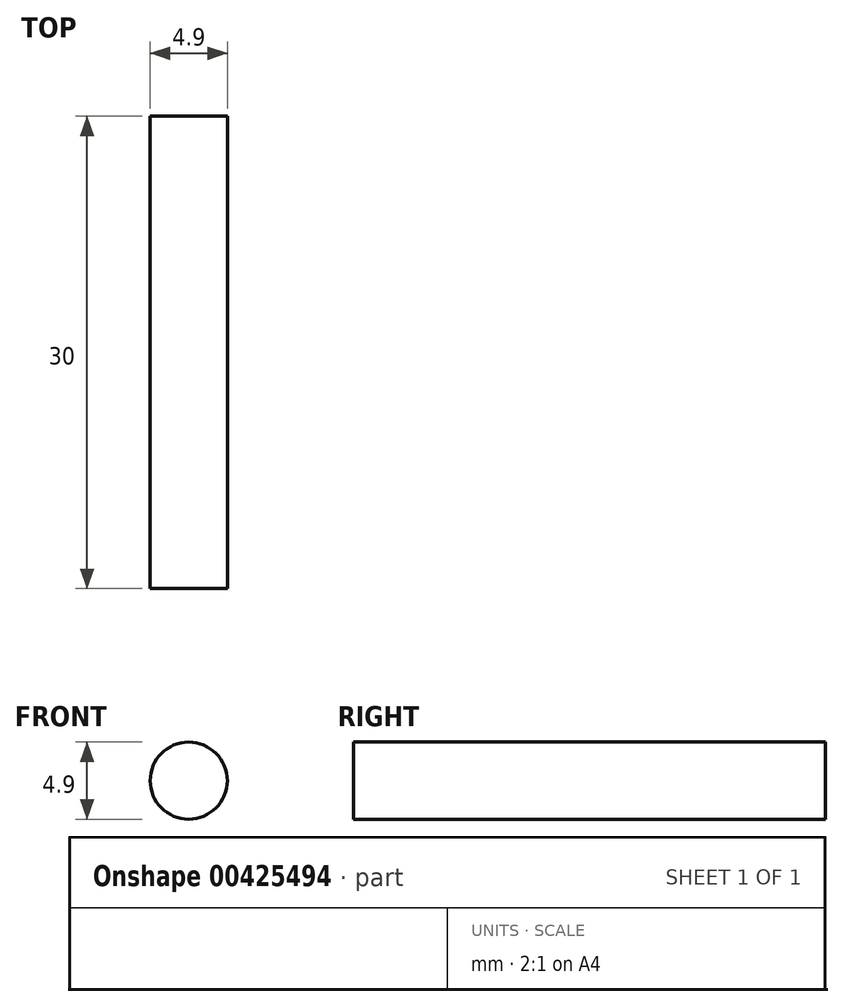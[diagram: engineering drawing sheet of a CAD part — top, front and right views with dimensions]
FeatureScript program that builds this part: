
annotation { "Feature Type Name" : "Feature", "Feature Type Description" : "" }
export const myFeature = defineFeature(function(context is Context, id is Id, definition is map)
    precondition{}
    {
        {
            var Q0;
            Q0=qCreatedBy(makeId("Front.planeOp"),FACE);
            var sketch = newSketch(context, id + "F0", { "sketchPlane" : qUnion([Q0])});
            skCircle(sketch, "E0", {"center": v(0, 0) * mm, "radius": 2.45 * mm});
            skSolve(sketch);
        }
        {
            var Q0;
            Q0=makeQuery(id+"F0.imprint","IMPRINT",FACE,{"disambiguationData":[TD([[makeQuery(id+"F0.imprint","IMPRINT",EDGE,{"derivedFrom":sQuery(id+"F0.wireOp",EDGE,"E0")}),1.0]])]});
            extrude(context, id + "F1", {"entities" : qUnion([Q0]), "depth" : 30 * mm});
        }
    });
